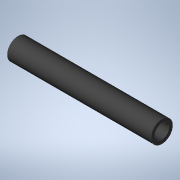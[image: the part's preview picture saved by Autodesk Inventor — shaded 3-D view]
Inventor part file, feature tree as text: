
AUTODESK INVENTOR PART (.ipt)
format: ipt  version: 2021.2 (Build 252289000, 289)  size: 106,496 bytes
history: native  units: in
note: dims shown in document units (in); Inventor stores cm internally (conversion verified against a paired STEP export)
features: direct_edit x2, move_body x2, extrude x1
ambient origin geometry x8: Origin, YZ Plane, XZ Plane, XY Plane, X Axis, Y Axis, Z Axis, Center Point
bodies: Solid1 (feature_tree)
feature tree (5):
  direct_edit  "Direct Edit1"
  direct_edit  "Direct Edit2"
  extrude  "Extrude1"  TaperAngle=0.0deg  [1 undecoded]
  move_body  "Move1"
  move_body  "Move2"
note: 1 required parameter value undecoded (feature->parameter linkage not recoverable at this tier; creation-order binding heuristic only, values carry confidence <= 0.55)
